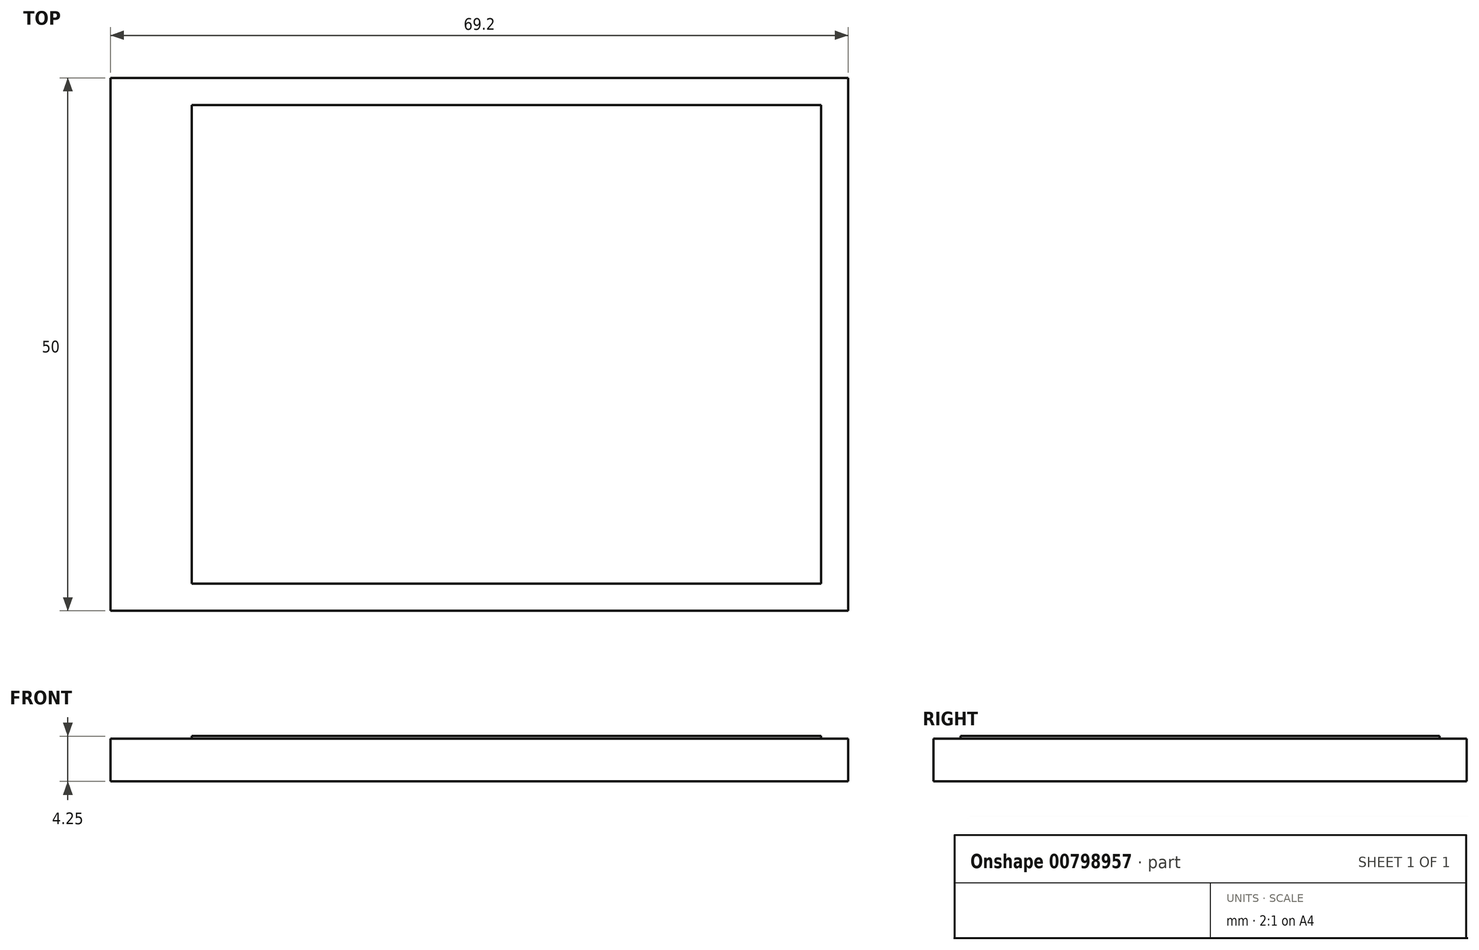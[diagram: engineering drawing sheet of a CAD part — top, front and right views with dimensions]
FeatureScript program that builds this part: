
annotation { "Feature Type Name" : "Feature", "Feature Type Description" : "" }
export const myFeature = defineFeature(function(context is Context, id is Id, definition is map)
    precondition{}
    {
        {
            var Q0;
            Q0=qCreatedBy(makeId("Top.planeOp"),FACE);
            var sketch = newSketch(context, id + "F0", { "sketchPlane" : qUnion([Q0])});
            skLineSegment(sketch, "E0.bottom", {"start": v(-43, 28) * mm, "end": v(43, 28) * mm});
            skLineSegment(sketch, "E0.top", {"start": v(-43, -28) * mm, "end": v(43, -28) * mm});
            skLineSegment(sketch, "E0.left", {"start": v(-43, 28) * mm, "end": v(-43, -28) * mm});
            skLineSegment(sketch, "E0.right", {"start": v(43, 28) * mm, "end": v(43, -28) * mm});
            skCircle(sketch, "E1", {"center": v(-39.4, 24.4) * mm, "radius": 2.54 * mm});
            skCircle(sketch, "E2", {"center": v(-39.4, -24.4) * mm, "radius": 2.54 * mm});
            skCircle(sketch, "E3", {"center": v(39.4, 24.4) * mm, "radius": 2.54 * mm});
            skSolve(sketch);
        }
        {
            var Q0;
            Q0 = qSketchRegion(id + "F0", true);
            extrude(context, id + "F1", {"entities" : qUnion([Q0]), "depth" : -2.03 * mm, "offsetDistance" : 25.4 * mm});
        }
        {
            var Q0;
            Q0=qCreatedBy(makeId("Top.planeOp"),FACE);
            var sketch = newSketch(context, id + "F2", { "sketchPlane" : qUnion([Q0])});
            skLineSegment(sketch, "E4.bottom", {"start": v(-36, 28) * mm, "end": v(33.2, 28) * mm});
            skLineSegment(sketch, "E4.top", {"start": v(-36, -22) * mm, "end": v(33.2, -22) * mm});
            skLineSegment(sketch, "E4.left", {"start": v(-36, 28) * mm, "end": v(-36, -22) * mm});
            skLineSegment(sketch, "E4.right", {"start": v(33.2, 28) * mm, "end": v(33.2, -22) * mm});
            skSolve(sketch);
        }
        {
            var Q0;
            Q0 = qSketchRegion(id + "F2", true);
            extrude(context, id + "F3", {"entities" : qUnion([Q0]), "depth" : 4 * mm, "offsetDistance" : 25.4 * mm});
        }
        {
            var Q0;
            Q0=makeQuery(id+"F0.imprint","IMPRINT",FACE,{"disambiguationData":[TD([[makeQuery(id+"F0.imprint","IMPRINT",EDGE,{"derivedFrom":sQuery(id+"F0.wireOp",EDGE,"E0.bottom")}),-1.0]])]});
            var Q1;
            Q1=sQuery(id+"F0.wireOp",EDGE,"E1");
            var Q2;
            Q2=sQuery(id+"F0.wireOp",EDGE,"E2");
            var Q3;
            Q3=sQuery(id+"F0.wireOp",EDGE,"E3");
            extrude(context, id + "F4", {"entities" : qUnion([Q0]), "operationType" : NewBodyOperationType.REMOVE, "surfaceEntities" : qUnion([Q1, Q2, Q3]), "oppositeDirection" : true, "depth" : 25.4 * mm, "offsetDistance" : 25.4 * mm});
        }
        {
            var Q0;
            Q0=makeQuery(id+"F3.opExtrude","CAP_FACE",FACE,{"disambiguationData":[OSD([sQuery(id+"F2.wireOp",EDGE,"E4.bottom"),sQuery(id+"F2.wireOp",EDGE,"E4.top"),sQuery(id+"F2.wireOp",EDGE,"E4.left"),sQuery(id+"F2.wireOp",EDGE,"E4.right")])],"isStart":false});
            var sketch = newSketch(context, id + "F5", { "sketchPlane" : qUnion([Q0])});
            skLineSegment(sketch, "E5.bottom", {"start": v(-28.38, 25.46) * mm, "end": v(30.66, 25.46) * mm});
            skLineSegment(sketch, "E5.top", {"start": v(-28.38, -19.46) * mm, "end": v(30.66, -19.46) * mm});
            skLineSegment(sketch, "E5.left", {"start": v(-28.38, 25.46) * mm, "end": v(-28.38, -19.46) * mm});
            skLineSegment(sketch, "E5.right", {"start": v(30.66, 25.46) * mm, "end": v(30.66, -19.46) * mm});
            skSolve(sketch);
        }
        {
            var Q0;
            Q0=makeQuery(id+"F5.imprint","IMPRINT",FACE,{"disambiguationData":[TD([[makeQuery(id+"F5.imprint","IMPRINT",EDGE,{"derivedFrom":sQuery(id+"F5.wireOp",EDGE,"E5.bottom")}),-1.0]])]});
            extrude(context, id + "F6", {"entities" : qUnion([Q0]), "operationType" : NewBodyOperationType.ADD, "depth" : 0.25 * mm, "offsetDistance" : 25.4 * mm});
        }
    });
